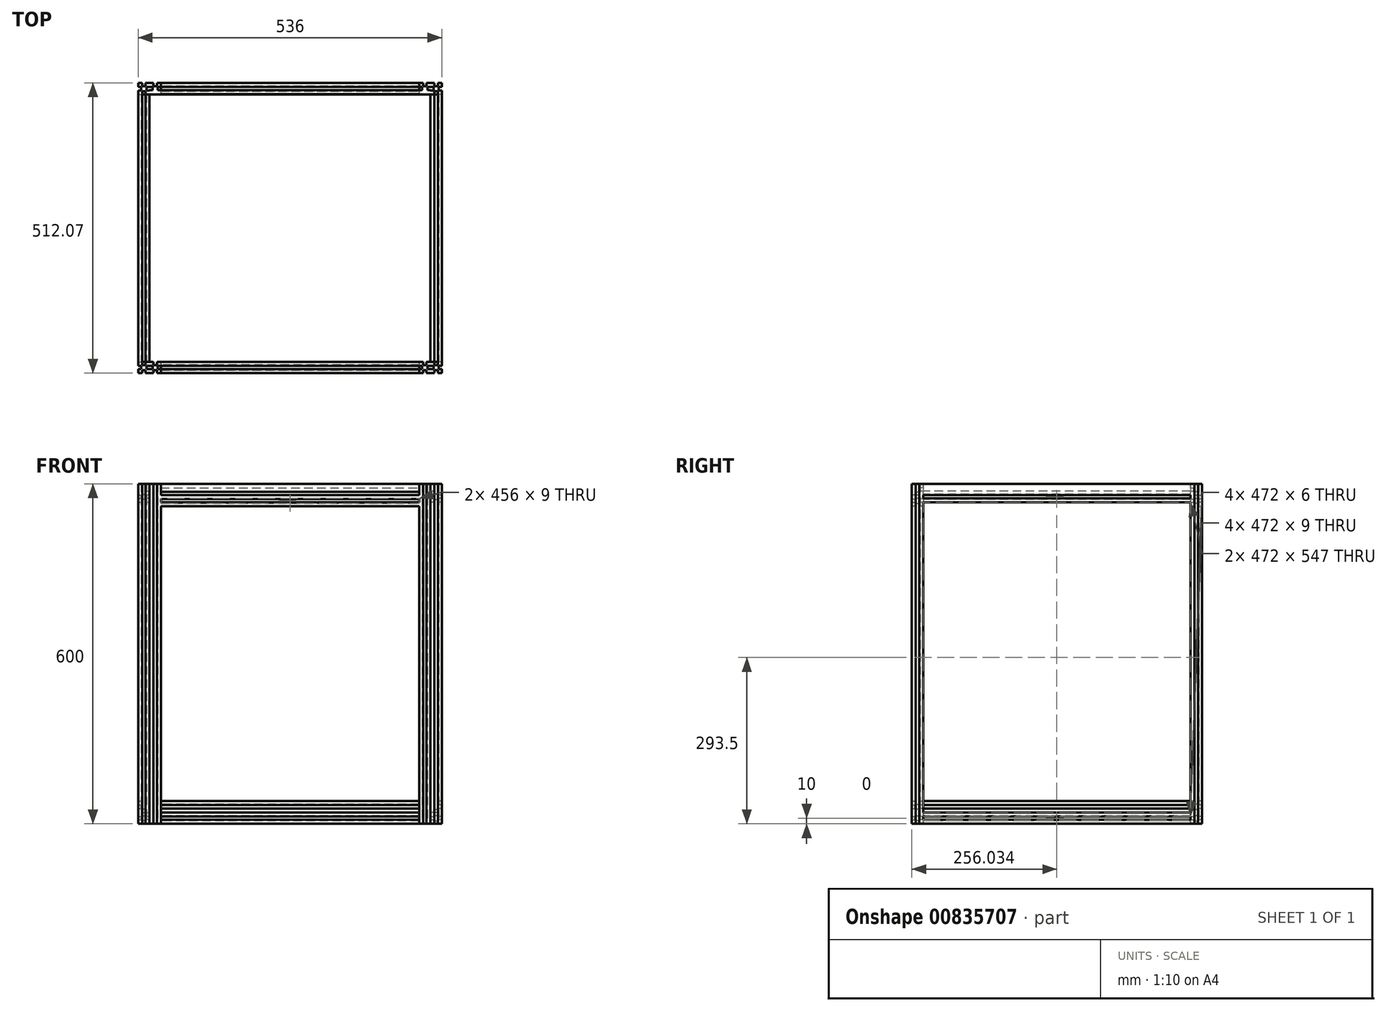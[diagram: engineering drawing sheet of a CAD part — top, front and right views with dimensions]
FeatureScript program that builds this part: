
annotation { "Feature Type Name" : "Feature", "Feature Type Description" : "" }
export const myFeature = defineFeature(function(context is Context, id is Id, definition is map)
    precondition{}
    {
        {
            var Q0;
            Q0=qCreatedBy(makeId("Right.planeOp"),FACE);
            var sketch = newSketch(context, id + "F0", { "sketchPlane" : qUnion([Q0])});
            skLineSegment(sketch, "E0.bottom", {"start": v(-73.97, 127.1) * mm, "end": v(-53.97, 127.1) * mm});
            skLineSegment(sketch, "E0.top", {"start": v(-73.97, 147.1) * mm, "end": v(-53.97, 147.1) * mm});
            skLineSegment(sketch, "E0.left", {"start": v(-73.97, 127.1) * mm, "end": v(-73.97, 147.1) * mm});
            skLineSegment(sketch, "E0.right", {"start": v(-53.97, 127.1) * mm, "end": v(-53.97, 147.1) * mm});
            skLineSegment(sketch, "E1.bottom", {"start": v(-66.97, 147.1) * mm, "end": v(-60.97, 147.1) * mm});
            skLineSegment(sketch, "E1.top", {"start": v(-66.97, 141.6) * mm, "end": v(-60.97, 141.6) * mm});
            skLineSegment(sketch, "E1.left", {"start": v(-66.97, 147.1) * mm, "end": v(-66.97, 141.6) * mm});
            skLineSegment(sketch, "E1.right", {"start": v(-60.97, 147.1) * mm, "end": v(-60.97, 141.6) * mm});
            skLineSegment(sketch, "E2.bottom", {"start": v(-53.97, 140.1) * mm, "end": v(-59.47, 140.1) * mm});
            skLineSegment(sketch, "E2.top", {"start": v(-53.97, 134.1) * mm, "end": v(-59.47, 134.1) * mm});
            skLineSegment(sketch, "E2.left", {"start": v(-53.97, 140.1) * mm, "end": v(-53.97, 134.1) * mm});
            skLineSegment(sketch, "E2.right", {"start": v(-59.47, 140.1) * mm, "end": v(-59.47, 134.1) * mm});
            skLineSegment(sketch, "E3.bottom", {"start": v(-60.97, 127.1) * mm, "end": v(-66.97, 127.1) * mm});
            skLineSegment(sketch, "E3.top", {"start": v(-60.97, 132.6) * mm, "end": v(-66.97, 132.6) * mm});
            skLineSegment(sketch, "E3.left", {"start": v(-60.97, 127.1) * mm, "end": v(-60.97, 132.6) * mm});
            skLineSegment(sketch, "E3.right", {"start": v(-66.97, 127.1) * mm, "end": v(-66.97, 132.6) * mm});
            skLineSegment(sketch, "E4.bottom", {"start": v(-73.97, 134.1) * mm, "end": v(-68.47, 134.1) * mm});
            skLineSegment(sketch, "E4.top", {"start": v(-73.97, 140.1) * mm, "end": v(-68.47, 140.1) * mm});
            skLineSegment(sketch, "E4.left", {"start": v(-73.97, 134.1) * mm, "end": v(-73.97, 140.1) * mm});
            skLineSegment(sketch, "E4.right", {"start": v(-68.47, 134.1) * mm, "end": v(-68.47, 140.1) * mm});
            skLineSegment(sketch, "E5.bottom", {"start": v(-74.01, 107.1) * mm, "end": v(-54.01, 107.1) * mm});
            skLineSegment(sketch, "E5.top", {"start": v(-74.01, 127.1) * mm, "end": v(-54.01, 127.1) * mm});
            skLineSegment(sketch, "E5.left", {"start": v(-74.01, 107.1) * mm, "end": v(-74.01, 127.1) * mm});
            skLineSegment(sketch, "E5.right", {"start": v(-54.01, 107.1) * mm, "end": v(-54.01, 127.1) * mm});
            skLineSegment(sketch, "E6.bottom", {"start": v(-67.01, 127.1) * mm, "end": v(-61.01, 127.1) * mm});
            skLineSegment(sketch, "E6.top", {"start": v(-67.01, 121.6) * mm, "end": v(-61.01, 121.6) * mm});
            skLineSegment(sketch, "E6.left", {"start": v(-67.01, 127.1) * mm, "end": v(-67.01, 121.6) * mm});
            skLineSegment(sketch, "E6.right", {"start": v(-61.01, 127.1) * mm, "end": v(-61.01, 121.6) * mm});
            skLineSegment(sketch, "E7.bottom", {"start": v(-54.01, 120.1) * mm, "end": v(-59.51, 120.1) * mm});
            skLineSegment(sketch, "E7.top", {"start": v(-54.01, 114.1) * mm, "end": v(-59.51, 114.1) * mm});
            skLineSegment(sketch, "E7.left", {"start": v(-54.01, 120.1) * mm, "end": v(-54.01, 114.1) * mm});
            skLineSegment(sketch, "E7.right", {"start": v(-59.51, 120.1) * mm, "end": v(-59.51, 114.1) * mm});
            skLineSegment(sketch, "E8.bottom", {"start": v(-61.01, 107.1) * mm, "end": v(-67.01, 107.1) * mm});
            skLineSegment(sketch, "E8.top", {"start": v(-61.01, 112.6) * mm, "end": v(-67.01, 112.6) * mm});
            skLineSegment(sketch, "E8.left", {"start": v(-61.01, 107.1) * mm, "end": v(-61.01, 112.6) * mm});
            skLineSegment(sketch, "E8.right", {"start": v(-67.01, 107.1) * mm, "end": v(-67.01, 112.6) * mm});
            skLineSegment(sketch, "E9.bottom", {"start": v(-74.01, 114.1) * mm, "end": v(-68.51, 114.1) * mm});
            skLineSegment(sketch, "E9.top", {"start": v(-74.01, 120.1) * mm, "end": v(-68.51, 120.1) * mm});
            skLineSegment(sketch, "E9.left", {"start": v(-74.01, 114.1) * mm, "end": v(-74.01, 120.1) * mm});
            skLineSegment(sketch, "E9.right", {"start": v(-68.51, 114.1) * mm, "end": v(-68.51, 120.1) * mm});
            skSolve(sketch);
        }
        {
            var Q0;
            {var subQ11=sQuery(id+"F0.wireOp",EDGE,"E0.bottom");Q0=makeQuery(id+"F0.imprint","IMPRINT",FACE,{"disambiguationData":[TD([[makeQuery(id+"F0.imprint","IMPRINT",EDGE,{"derivedFrom":subQ11}),1.0]])]});}
            var Q1;
            Q1=makeQuery(id+"F0.imprint","IMPRINT",FACE,{"disambiguationData":[TD([[makeQuery(id+"F0.imprint","IMPRINT",EDGE,{"derivedFrom":sQuery(id+"F0.wireOp",EDGE,"E6.top")}),-1.0]])]});
            extrude(context, id + "F1", {"entities" : qUnion([Q0, Q1]), "depth" : 270 * mm, "offsetDistance" : 25 * mm});
        }
        {
            var Q0;
            {var subQ0=sQuery(id+"F0.wireOp",EDGE,"E5.bottom");var subQ1=makeQuery(id+"F1.opExtrude","SWEPT_FACE",FACE,{"disambiguationData":[OSD([subQ0]),TDD([makeQuery(id+"F0.imprint","IMPRINT",EDGE,{"disambiguationData":[TD([[makeQuery(id+"F0.imprint","INTERSECT",VERTEX,{"derivedFrom":[subQ0,sQuery(id+"F0.wireOp",EDGE,"E5.left")]}),-1.0]])],"derivedFrom":subQ0})])]});Q0=makeQuery(id+"FbfQmAbu5wMZM1G_1.boolean.opBoolean","MERGE",FACE,{"derivedFrom":[subQ1,makeQuery(id+"FbfQmAbu5wMZM1G_1.opPattern","COPY",FACE,{"derivedFrom":subQ1,"instanceName":"1"})]});}
            var sketch = newSketch(context, id + "F2", { "sketchPlane" : qUnion([Q0])});
            skLineSegment(sketch, "E10.bottom", {"start": v(290, 54.12) * mm, "end": v(290, 74.12) * mm});
            skLineSegment(sketch, "E10.top", {"start": v(270, 54.12) * mm, "end": v(270, 74.12) * mm});
            skLineSegment(sketch, "E10.left", {"start": v(290, 54.12) * mm, "end": v(270, 54.12) * mm});
            skLineSegment(sketch, "E10.right", {"start": v(290, 74.12) * mm, "end": v(270, 74.12) * mm});
            skLineSegment(sketch, "E11.bottom", {"start": v(270, 61.12) * mm, "end": v(270, 67.12) * mm});
            skLineSegment(sketch, "E11.top", {"start": v(275.5, 61.12) * mm, "end": v(275.5, 67.12) * mm});
            skLineSegment(sketch, "E11.left", {"start": v(270, 61.12) * mm, "end": v(275.5, 61.12) * mm});
            skLineSegment(sketch, "E11.right", {"start": v(270, 67.12) * mm, "end": v(275.5, 67.12) * mm});
            skLineSegment(sketch, "E12.bottom", {"start": v(277, 74.12) * mm, "end": v(277, 68.62) * mm});
            skLineSegment(sketch, "E12.top", {"start": v(283, 74.12) * mm, "end": v(283, 68.62) * mm});
            skLineSegment(sketch, "E12.left", {"start": v(277, 74.12) * mm, "end": v(283, 74.12) * mm});
            skLineSegment(sketch, "E12.right", {"start": v(277, 68.62) * mm, "end": v(283, 68.62) * mm});
            skLineSegment(sketch, "E13.bottom", {"start": v(290, 67.12) * mm, "end": v(290, 61.12) * mm});
            skLineSegment(sketch, "E13.top", {"start": v(284.5, 67.12) * mm, "end": v(284.5, 61.12) * mm});
            skLineSegment(sketch, "E13.left", {"start": v(290, 67.12) * mm, "end": v(284.5, 67.12) * mm});
            skLineSegment(sketch, "E13.right", {"start": v(290, 61.12) * mm, "end": v(284.5, 61.12) * mm});
            skLineSegment(sketch, "E14.bottom", {"start": v(283, 54.12) * mm, "end": v(283, 59.62) * mm});
            skLineSegment(sketch, "E14.top", {"start": v(277, 54.12) * mm, "end": v(277, 59.62) * mm});
            skLineSegment(sketch, "E14.left", {"start": v(283, 54.12) * mm, "end": v(277, 54.12) * mm});
            skLineSegment(sketch, "E14.right", {"start": v(283, 59.62) * mm, "end": v(277, 59.62) * mm});
            skLineSegment(sketch, "E15.bottom", {"start": v(310, 54.09) * mm, "end": v(310, 74.09) * mm});
            skLineSegment(sketch, "E15.top", {"start": v(290, 54.09) * mm, "end": v(290, 74.09) * mm});
            skLineSegment(sketch, "E15.left", {"start": v(310, 54.09) * mm, "end": v(290, 54.09) * mm});
            skLineSegment(sketch, "E15.right", {"start": v(310, 74.09) * mm, "end": v(290, 74.09) * mm});
            skLineSegment(sketch, "E16.bottom", {"start": v(290, 61.09) * mm, "end": v(290, 67.09) * mm});
            skLineSegment(sketch, "E16.top", {"start": v(295.5, 61.09) * mm, "end": v(295.5, 67.09) * mm});
            skLineSegment(sketch, "E16.left", {"start": v(290, 61.09) * mm, "end": v(295.5, 61.09) * mm});
            skLineSegment(sketch, "E16.right", {"start": v(290, 67.09) * mm, "end": v(295.5, 67.09) * mm});
            skLineSegment(sketch, "E17.bottom", {"start": v(297, 74.09) * mm, "end": v(297, 68.59) * mm});
            skLineSegment(sketch, "E17.top", {"start": v(303, 74.09) * mm, "end": v(303, 68.59) * mm});
            skLineSegment(sketch, "E17.left", {"start": v(297, 74.09) * mm, "end": v(303, 74.09) * mm});
            skLineSegment(sketch, "E17.right", {"start": v(297, 68.59) * mm, "end": v(303, 68.59) * mm});
            skLineSegment(sketch, "E18.bottom", {"start": v(310, 67.09) * mm, "end": v(310, 61.09) * mm});
            skLineSegment(sketch, "E18.top", {"start": v(304.5, 67.09) * mm, "end": v(304.5, 61.09) * mm});
            skLineSegment(sketch, "E18.left", {"start": v(310, 67.09) * mm, "end": v(304.5, 67.09) * mm});
            skLineSegment(sketch, "E18.right", {"start": v(310, 61.09) * mm, "end": v(304.5, 61.09) * mm});
            skLineSegment(sketch, "E19.bottom", {"start": v(303, 54.09) * mm, "end": v(303, 59.59) * mm});
            skLineSegment(sketch, "E19.top", {"start": v(297, 54.09) * mm, "end": v(297, 59.59) * mm});
            skLineSegment(sketch, "E19.left", {"start": v(303, 54.09) * mm, "end": v(297, 54.09) * mm});
            skLineSegment(sketch, "E19.right", {"start": v(303, 59.59) * mm, "end": v(297, 59.59) * mm});
            skSolve(sketch);
        }
        {
            var Q0;
            Q0=makeQuery(id+"F2.imprint","IMPRINT",FACE,{"disambiguationData":[TD([[makeQuery(id+"F2.imprint","IMPRINT",EDGE,{"derivedFrom":sQuery(id+"F2.wireOp",EDGE,"E16.top")}),-1.0]])]});
            var Q1;
            {var subQ16=sQuery(id+"F2.wireOp",EDGE,"E10.bottom");Q1=makeQuery(id+"F2.imprint","IMPRINT",FACE,{"disambiguationData":[TD([[makeQuery(id+"F2.imprint","IMPRINT",EDGE,{"derivedFrom":subQ16}),1.0]])]});}
            extrude(context, id + "F3", {"entities" : qUnion([Q0, Q1]), "operationType" : NewBodyOperationType.ADD, "oppositeDirection" : true, "depth" : 600 * mm, "offsetDistance" : 25 * mm});
        }
        {
            var Q0;
            {var subQ1=sQuery(id+"F2.wireOp",EDGE,"E10.left");var subQ2=sQuery(id+"F2.wireOp",EDGE,"E10.top");var subQ3=makeQuery(id+"F2.imprint","INTERSECT",VERTEX,{"derivedFrom":[subQ2,subQ1]});var subQ5=sQuery(id+"F0.wireOp",EDGE,"E1.top");Q0=makeQuery(id+"F3.boolean.opBoolean","SPLIT",FACE,{"disambiguationData":[TD([makeQuery(id+"F1.opExtrude","SWEPT_FACE",FACE,{"disambiguationData":[OSD([subQ5])]})])],"derivedFrom":makeQuery(id+"F3.opExtrude","SWEPT_FACE",FACE,{"disambiguationData":[OSD([subQ2]),TDD([makeQuery(id+"F2.imprint","IMPRINT",EDGE,{"disambiguationData":[TD([[subQ3,-1.0]])],"derivedFrom":subQ2})])]})});}
            var sketch = newSketch(context, id + "F4", { "sketchPlane" : qUnion([Q0])});
            skLineSegment(sketch, "E20.bottom", {"start": v(54.16, 687.1) * mm, "end": v(74.16, 687.1) * mm});
            skLineSegment(sketch, "E20.top", {"start": v(54.16, 707.1) * mm, "end": v(74.16, 707.1) * mm});
            skLineSegment(sketch, "E20.left", {"start": v(54.16, 687.1) * mm, "end": v(54.16, 707.1) * mm});
            skLineSegment(sketch, "E20.right", {"start": v(74.16, 687.1) * mm, "end": v(74.16, 707.1) * mm});
            skLineSegment(sketch, "E21.bottom", {"start": v(61.16, 707.1) * mm, "end": v(67.16, 707.1) * mm});
            skLineSegment(sketch, "E21.top", {"start": v(61.16, 701.6) * mm, "end": v(67.16, 701.6) * mm});
            skLineSegment(sketch, "E21.left", {"start": v(61.16, 707.1) * mm, "end": v(61.16, 701.6) * mm});
            skLineSegment(sketch, "E21.right", {"start": v(67.16, 707.1) * mm, "end": v(67.16, 701.6) * mm});
            skLineSegment(sketch, "E22.bottom", {"start": v(74.16, 700.1) * mm, "end": v(68.66, 700.1) * mm});
            skLineSegment(sketch, "E22.top", {"start": v(74.16, 694.1) * mm, "end": v(68.66, 694.1) * mm});
            skLineSegment(sketch, "E22.left", {"start": v(74.16, 700.1) * mm, "end": v(74.16, 694.1) * mm});
            skLineSegment(sketch, "E22.right", {"start": v(68.66, 700.1) * mm, "end": v(68.66, 694.1) * mm});
            skLineSegment(sketch, "E23.bottom", {"start": v(67.16, 687.1) * mm, "end": v(61.16, 687.1) * mm});
            skLineSegment(sketch, "E23.top", {"start": v(67.16, 692.6) * mm, "end": v(61.16, 692.6) * mm});
            skLineSegment(sketch, "E23.left", {"start": v(67.16, 687.1) * mm, "end": v(67.16, 692.6) * mm});
            skLineSegment(sketch, "E23.right", {"start": v(61.16, 687.1) * mm, "end": v(61.16, 692.6) * mm});
            skLineSegment(sketch, "E24.bottom", {"start": v(54.16, 694.1) * mm, "end": v(59.66, 694.1) * mm});
            skLineSegment(sketch, "E24.top", {"start": v(54.16, 700.1) * mm, "end": v(59.66, 700.1) * mm});
            skLineSegment(sketch, "E24.left", {"start": v(54.16, 694.1) * mm, "end": v(54.16, 700.1) * mm});
            skLineSegment(sketch, "E24.right", {"start": v(59.66, 694.1) * mm, "end": v(59.66, 700.1) * mm});
            skLineSegment(sketch, "E25.bottom", {"start": v(54.12, 667.1) * mm, "end": v(74.12, 667.1) * mm});
            skLineSegment(sketch, "E25.top", {"start": v(54.12, 687.1) * mm, "end": v(74.12, 687.1) * mm});
            skLineSegment(sketch, "E25.left", {"start": v(54.12, 667.1) * mm, "end": v(54.12, 687.1) * mm});
            skLineSegment(sketch, "E25.right", {"start": v(74.12, 667.1) * mm, "end": v(74.12, 687.1) * mm});
            skLineSegment(sketch, "E26.bottom", {"start": v(61.12, 687.1) * mm, "end": v(67.12, 687.1) * mm});
            skLineSegment(sketch, "E26.top", {"start": v(61.12, 681.6) * mm, "end": v(67.12, 681.6) * mm});
            skLineSegment(sketch, "E26.left", {"start": v(61.12, 687.1) * mm, "end": v(61.12, 681.6) * mm});
            skLineSegment(sketch, "E26.right", {"start": v(67.12, 687.1) * mm, "end": v(67.12, 681.6) * mm});
            skLineSegment(sketch, "E27.bottom", {"start": v(74.12, 680.1) * mm, "end": v(68.62, 680.1) * mm});
            skLineSegment(sketch, "E27.top", {"start": v(74.12, 674.1) * mm, "end": v(68.62, 674.1) * mm});
            skLineSegment(sketch, "E27.left", {"start": v(74.12, 680.1) * mm, "end": v(74.12, 674.1) * mm});
            skLineSegment(sketch, "E27.right", {"start": v(68.62, 680.1) * mm, "end": v(68.62, 674.1) * mm});
            skLineSegment(sketch, "E28.bottom", {"start": v(67.12, 667.1) * mm, "end": v(61.12, 667.1) * mm});
            skLineSegment(sketch, "E28.top", {"start": v(67.12, 672.6) * mm, "end": v(61.12, 672.6) * mm});
            skLineSegment(sketch, "E28.left", {"start": v(67.12, 667.1) * mm, "end": v(67.12, 672.6) * mm});
            skLineSegment(sketch, "E28.right", {"start": v(61.12, 667.1) * mm, "end": v(61.12, 672.6) * mm});
            skLineSegment(sketch, "E29.bottom", {"start": v(54.12, 674.1) * mm, "end": v(59.62, 674.1) * mm});
            skLineSegment(sketch, "E29.top", {"start": v(54.12, 680.1) * mm, "end": v(59.62, 680.1) * mm});
            skLineSegment(sketch, "E29.left", {"start": v(54.12, 674.1) * mm, "end": v(54.12, 680.1) * mm});
            skLineSegment(sketch, "E29.right", {"start": v(59.62, 674.1) * mm, "end": v(59.62, 680.1) * mm});
            skSolve(sketch);
        }
        {
            var Q0;
            {var subQ10=sQuery(id+"F4.wireOp",EDGE,"E24.bottom");Q0=makeQuery(id+"F4.imprint","IMPRINT",FACE,{"disambiguationData":[TD([[makeQuery(id+"F4.imprint","IMPRINT",EDGE,{"derivedFrom":subQ10}),-1.0]])]});}
            var Q1;
            {var subQ20=sQuery(id+"F4.wireOp",EDGE,"E20.bottom");Q1=makeQuery(id+"F4.imprint","IMPRINT",FACE,{"disambiguationData":[TD([[makeQuery(id+"F4.imprint","IMPRINT",EDGE,{"derivedFrom":subQ20}),1.0]])]});}
            var Q2;
            {var subQ6=sQuery(id+"F4.wireOp",EDGE,"E26.top");Q2=makeQuery(id+"F4.imprint","IMPRINT",FACE,{"disambiguationData":[TD([[makeQuery(id+"F4.imprint","IMPRINT",EDGE,{"derivedFrom":subQ6}),-1.0]])]});}
            var Q3;
            {var subQ2=sQuery(id+"F4.wireOp",EDGE,"E26.left");Q3=makeQuery(id+"F4.imprint","IMPRINT",FACE,{"disambiguationData":[TD([[makeQuery(id+"F4.imprint","IMPRINT",EDGE,{"derivedFrom":subQ2}),-1.0]])]});}
            extrude(context, id + "F5", {"entities" : qUnion([Q0, Q1, Q2, Q3]), "operationType" : NewBodyOperationType.ADD, "depth" : 228 * mm, "offsetDistance" : 25 * mm});
        }
        {
            var Q0;
            {var subQ0=sQuery(id+"F2.wireOp",EDGE,"E15.left");Q0=makeQuery(id+"F3.opExtrude","SWEPT_FACE",FACE,{"disambiguationData":[OSD([subQ0]),TDD([makeQuery(id+"F2.imprint","IMPRINT",EDGE,{"disambiguationData":[TD([[makeQuery(id+"F2.imprint","INTERSECT",VERTEX,{"derivedFrom":[sQuery(id+"F2.wireOp",EDGE,"E15.bottom"),subQ0]}),-1.0]])],"derivedFrom":subQ0})])]});}
            var sketch = newSketch(context, id + "F6", { "sketchPlane" : qUnion([Q0])});
            skLineSegment(sketch, "E30.bottom", {"start": v(-309.96, 694.1) * mm, "end": v(-289.96, 694.1) * mm});
            skLineSegment(sketch, "E31.bottom", {"start": v(-296.96, 694.1) * mm, "end": v(-302.96, 694.1) * mm});
            skLineSegment(sketch, "E32.bottom", {"start": v(-310, 674.1) * mm, "end": v(-290, 674.1) * mm});
            skLineSegment(sketch, "E32.top", {"start": v(-310, 694.1) * mm, "end": v(-290, 694.1) * mm});
            skLineSegment(sketch, "E32.left", {"start": v(-310, 674.1) * mm, "end": v(-310, 694.1) * mm});
            skLineSegment(sketch, "E32.right", {"start": v(-290, 674.1) * mm, "end": v(-290, 694.1) * mm});
            skLineSegment(sketch, "E33.bottom", {"start": v(-303, 694.1) * mm, "end": v(-297, 694.1) * mm});
            skLineSegment(sketch, "E33.top", {"start": v(-303, 688.6) * mm, "end": v(-297, 688.6) * mm});
            skLineSegment(sketch, "E33.left", {"start": v(-303, 694.1) * mm, "end": v(-303, 688.6) * mm});
            skLineSegment(sketch, "E33.right", {"start": v(-297, 694.1) * mm, "end": v(-297, 688.6) * mm});
            skLineSegment(sketch, "E34.bottom", {"start": v(-290, 687.1) * mm, "end": v(-295.5, 687.1) * mm});
            skLineSegment(sketch, "E34.top", {"start": v(-290, 681.1) * mm, "end": v(-295.5, 681.1) * mm});
            skLineSegment(sketch, "E34.left", {"start": v(-290, 687.1) * mm, "end": v(-290, 681.1) * mm});
            skLineSegment(sketch, "E34.right", {"start": v(-295.5, 687.1) * mm, "end": v(-295.5, 681.1) * mm});
            skLineSegment(sketch, "E35.bottom", {"start": v(-297, 674.1) * mm, "end": v(-303, 674.1) * mm});
            skLineSegment(sketch, "E35.top", {"start": v(-297, 679.6) * mm, "end": v(-303, 679.6) * mm});
            skLineSegment(sketch, "E35.left", {"start": v(-297, 674.1) * mm, "end": v(-297, 679.6) * mm});
            skLineSegment(sketch, "E35.right", {"start": v(-303, 674.1) * mm, "end": v(-303, 679.6) * mm});
            skLineSegment(sketch, "E36.bottom", {"start": v(-310, 681.1) * mm, "end": v(-304.5, 681.1) * mm});
            skLineSegment(sketch, "E36.top", {"start": v(-310, 687.1) * mm, "end": v(-304.5, 687.1) * mm});
            skLineSegment(sketch, "E36.left", {"start": v(-310, 681.1) * mm, "end": v(-310, 687.1) * mm});
            skLineSegment(sketch, "E36.right", {"start": v(-304.5, 681.1) * mm, "end": v(-304.5, 687.1) * mm});
            skLineSegment(sketch, "E37.bottom", {"start": v(-309.96, 127.1) * mm, "end": v(-289.96, 127.1) * mm});
            skLineSegment(sketch, "E37.top", {"start": v(-309.96, 147.1) * mm, "end": v(-289.96, 147.1) * mm});
            skLineSegment(sketch, "E37.left", {"start": v(-309.96, 127.1) * mm, "end": v(-309.96, 147.1) * mm});
            skLineSegment(sketch, "E37.right", {"start": v(-289.96, 127.1) * mm, "end": v(-289.96, 147.1) * mm});
            skLineSegment(sketch, "E38.bottom", {"start": v(-302.96, 147.1) * mm, "end": v(-296.96, 147.1) * mm});
            skLineSegment(sketch, "E38.top", {"start": v(-302.96, 141.6) * mm, "end": v(-296.96, 141.6) * mm});
            skLineSegment(sketch, "E38.left", {"start": v(-302.96, 147.1) * mm, "end": v(-302.96, 141.6) * mm});
            skLineSegment(sketch, "E38.right", {"start": v(-296.96, 147.1) * mm, "end": v(-296.96, 141.6) * mm});
            skLineSegment(sketch, "E39.bottom", {"start": v(-289.96, 140.1) * mm, "end": v(-295.46, 140.1) * mm});
            skLineSegment(sketch, "E39.top", {"start": v(-289.96, 134.1) * mm, "end": v(-295.46, 134.1) * mm});
            skLineSegment(sketch, "E39.left", {"start": v(-289.96, 140.1) * mm, "end": v(-289.96, 134.1) * mm});
            skLineSegment(sketch, "E39.right", {"start": v(-295.46, 140.1) * mm, "end": v(-295.46, 134.1) * mm});
            skLineSegment(sketch, "E40.bottom", {"start": v(-296.96, 127.1) * mm, "end": v(-302.96, 127.1) * mm});
            skLineSegment(sketch, "E40.top", {"start": v(-296.96, 132.6) * mm, "end": v(-302.96, 132.6) * mm});
            skLineSegment(sketch, "E40.left", {"start": v(-296.96, 127.1) * mm, "end": v(-296.96, 132.6) * mm});
            skLineSegment(sketch, "E40.right", {"start": v(-302.96, 127.1) * mm, "end": v(-302.96, 132.6) * mm});
            skLineSegment(sketch, "E41.bottom", {"start": v(-309.96, 134.1) * mm, "end": v(-304.46, 134.1) * mm});
            skLineSegment(sketch, "E41.top", {"start": v(-309.96, 140.1) * mm, "end": v(-304.46, 140.1) * mm});
            skLineSegment(sketch, "E41.left", {"start": v(-309.96, 134.1) * mm, "end": v(-309.96, 140.1) * mm});
            skLineSegment(sketch, "E41.right", {"start": v(-304.46, 134.1) * mm, "end": v(-304.46, 140.1) * mm});
            skLineSegment(sketch, "E42.bottom", {"start": v(-310, 107.1) * mm, "end": v(-290, 107.1) * mm});
            skLineSegment(sketch, "E42.top", {"start": v(-310, 127.1) * mm, "end": v(-290, 127.1) * mm});
            skLineSegment(sketch, "E42.left", {"start": v(-310, 107.1) * mm, "end": v(-310, 127.1) * mm});
            skLineSegment(sketch, "E42.right", {"start": v(-290, 107.1) * mm, "end": v(-290, 127.1) * mm});
            skLineSegment(sketch, "E43.bottom", {"start": v(-303, 127.1) * mm, "end": v(-297, 127.1) * mm});
            skLineSegment(sketch, "E43.top", {"start": v(-303, 121.6) * mm, "end": v(-297, 121.6) * mm});
            skLineSegment(sketch, "E43.left", {"start": v(-303, 127.1) * mm, "end": v(-303, 121.6) * mm});
            skLineSegment(sketch, "E43.right", {"start": v(-297, 127.1) * mm, "end": v(-297, 121.6) * mm});
            skLineSegment(sketch, "E44.bottom", {"start": v(-290, 120.1) * mm, "end": v(-295.5, 120.1) * mm});
            skLineSegment(sketch, "E44.top", {"start": v(-290, 114.1) * mm, "end": v(-295.5, 114.1) * mm});
            skLineSegment(sketch, "E44.left", {"start": v(-290, 120.1) * mm, "end": v(-290, 114.1) * mm});
            skLineSegment(sketch, "E44.right", {"start": v(-295.5, 120.1) * mm, "end": v(-295.5, 114.1) * mm});
            skLineSegment(sketch, "E45.bottom", {"start": v(-297, 107.1) * mm, "end": v(-303, 107.1) * mm});
            skLineSegment(sketch, "E45.top", {"start": v(-297, 112.6) * mm, "end": v(-303, 112.6) * mm});
            skLineSegment(sketch, "E45.left", {"start": v(-297, 107.1) * mm, "end": v(-297, 112.6) * mm});
            skLineSegment(sketch, "E45.right", {"start": v(-303, 107.1) * mm, "end": v(-303, 112.6) * mm});
            skLineSegment(sketch, "E46.bottom", {"start": v(-310, 114.1) * mm, "end": v(-304.5, 114.1) * mm});
            skLineSegment(sketch, "E46.top", {"start": v(-310, 120.1) * mm, "end": v(-304.5, 120.1) * mm});
            skLineSegment(sketch, "E46.left", {"start": v(-310, 114.1) * mm, "end": v(-310, 120.1) * mm});
            skLineSegment(sketch, "E46.right", {"start": v(-304.5, 114.1) * mm, "end": v(-304.5, 120.1) * mm});
            skSolve(sketch);
        }
        {
            var Q0;
            {var subQ13=sQuery(id+"F6.wireOp",EDGE,"E37.bottom");Q0=makeQuery(id+"F6.imprint","IMPRINT",FACE,{"disambiguationData":[TD([[makeQuery(id+"F6.imprint","IMPRINT",EDGE,{"derivedFrom":subQ13}),1.0]])]});}
            var Q1;
            {var subQ5=sQuery(id+"F6.wireOp",EDGE,"E41.bottom");Q1=makeQuery(id+"F6.imprint","IMPRINT",FACE,{"disambiguationData":[TD([[makeQuery(id+"F6.imprint","IMPRINT",EDGE,{"derivedFrom":subQ5}),-1.0]])]});}
            var Q2;
            {var subQ2=sQuery(id+"F6.wireOp",EDGE,"E43.left");Q2=makeQuery(id+"F6.imprint","IMPRINT",FACE,{"disambiguationData":[TD([[makeQuery(id+"F6.imprint","IMPRINT",EDGE,{"derivedFrom":subQ2}),-1.0]])]});}
            var Q3;
            {var subQ6=sQuery(id+"F6.wireOp",EDGE,"E43.top");Q3=makeQuery(id+"F6.imprint","IMPRINT",FACE,{"disambiguationData":[TD([[makeQuery(id+"F6.imprint","IMPRINT",EDGE,{"derivedFrom":subQ6}),-1.0]])]});}
            var Q4;
            {var subQ12=sQuery(id+"F6.wireOp",EDGE,"9667445b-14a2-414e-8e40-848a2c53a070.bottom");Q4=makeQuery(id+"F6.imprint","IMPRINT",FACE,{"disambiguationData":[TD([[makeQuery(id+"F6.imprint","IMPRINT",EDGE,{"derivedFrom":subQ12}),-1.0]])]});}
            var Q5;
            {var subQ13=sQuery(id+"F6.wireOp",EDGE,"E30.bottom");Q5=makeQuery(id+"F6.imprint","IMPRINT",FACE,{"disambiguationData":[TD([[makeQuery(id+"F6.imprint","IMPRINT",EDGE,{"derivedFrom":subQ13}),1.0]])]});}
            var Q6;
            {var subQ6=sQuery(id+"F6.wireOp",EDGE,"E33.top");Q6=makeQuery(id+"F6.imprint","IMPRINT",FACE,{"disambiguationData":[TD([[makeQuery(id+"F6.imprint","IMPRINT",EDGE,{"derivedFrom":subQ6}),-1.0]])]});}
            var Q7;
            {var subQ2=sQuery(id+"F6.wireOp",EDGE,"E33.left");Q7=makeQuery(id+"F6.imprint","IMPRINT",FACE,{"disambiguationData":[TD([[makeQuery(id+"F6.imprint","IMPRINT",EDGE,{"derivedFrom":subQ2}),-1.0]])]});}
            extrude(context, id + "F7", {"entities" : qUnion([Q0, Q1, Q2, Q3, Q4, Q5, Q6, Q7]), "operationType" : NewBodyOperationType.ADD, "depth" : 236 * mm, "offsetDistance" : 25 * mm});
        }
        {
            var Q0;
            Q0=makeQuery(id+"F1.opExtrude","SWEPT_BODY",BODY,{"disambiguationData":[OSD([sQuery(id+"F0.wireOp",EDGE,"E0.bottom"),sQuery(id+"F0.wireOp",EDGE,"E0.top"),sQuery(id+"F0.wireOp",EDGE,"E0.left"),sQuery(id+"F0.wireOp",EDGE,"E0.right"),sQuery(id+"F0.wireOp",EDGE,"E1.top"),sQuery(id+"F0.wireOp",EDGE,"E1.left"),sQuery(id+"F0.wireOp",EDGE,"E1.right"),sQuery(id+"F0.wireOp",EDGE,"E2.bottom"),sQuery(id+"F0.wireOp",EDGE,"E2.top"),sQuery(id+"F0.wireOp",EDGE,"E2.right"),sQuery(id+"F0.wireOp",EDGE,"E3.top"),sQuery(id+"F0.wireOp",EDGE,"E3.left"),sQuery(id+"F0.wireOp",EDGE,"E3.right"),sQuery(id+"F0.wireOp",EDGE,"E4.bottom"),sQuery(id+"F0.wireOp",EDGE,"E4.top"),sQuery(id+"F0.wireOp",EDGE,"E4.right"),sQuery(id+"F0.wireOp",EDGE,"E5.bottom"),sQuery(id+"F0.wireOp",EDGE,"E5.top"),sQuery(id+"F0.wireOp",EDGE,"E5.left"),sQuery(id+"F0.wireOp",EDGE,"E5.right"),sQuery(id+"F0.wireOp",EDGE,"E6.bottom"),sQuery(id+"F0.wireOp",EDGE,"E6.top"),sQuery(id+"F0.wireOp",EDGE,"E6.left"),sQuery(id+"F0.wireOp",EDGE,"E6.right"),sQuery(id+"F0.wireOp",EDGE,"E7.bottom"),sQuery(id+"F0.wireOp",EDGE,"E7.top"),sQuery(id+"F0.wireOp",EDGE,"E7.right"),sQuery(id+"F0.wireOp",EDGE,"E8.top"),sQuery(id+"F0.wireOp",EDGE,"E8.left"),sQuery(id+"F0.wireOp",EDGE,"E8.right"),sQuery(id+"F0.wireOp",EDGE,"E9.bottom"),sQuery(id+"F0.wireOp",EDGE,"E9.top"),sQuery(id+"F0.wireOp",EDGE,"E9.right")])]});
            var Q1;
            Q1=makeQuery(id+"F7.opExtrude","CAP_FACE",FACE,{"disambiguationData":[OSD([sQuery(id+"F6.wireOp",EDGE,"E30.bottom"),sQuery(id+"F6.wireOp",EDGE,"E30.top"),sQuery(id+"F6.wireOp",EDGE,"E30.left"),sQuery(id+"F6.wireOp",EDGE,"E30.right"),sQuery(id+"F6.wireOp",EDGE,"697817fb-edbd-40a5-a29d-952f93a9c78b.top"),sQuery(id+"F6.wireOp",EDGE,"697817fb-edbd-40a5-a29d-952f93a9c78b.left"),sQuery(id+"F6.wireOp",EDGE,"697817fb-edbd-40a5-a29d-952f93a9c78b.right"),sQuery(id+"F6.wireOp",EDGE,"15fd4d5f-bd60-4fe3-bdb7-a61c8bb0770d.bottom"),sQuery(id+"F6.wireOp",EDGE,"15fd4d5f-bd60-4fe3-bdb7-a61c8bb0770d.top"),sQuery(id+"F6.wireOp",EDGE,"15fd4d5f-bd60-4fe3-bdb7-a61c8bb0770d.right"),sQuery(id+"F6.wireOp",EDGE,"E31.top"),sQuery(id+"F6.wireOp",EDGE,"E31.left"),sQuery(id+"F6.wireOp",EDGE,"E31.right"),sQuery(id+"F6.wireOp",EDGE,"9667445b-14a2-414e-8e40-848a2c53a070.bottom"),sQuery(id+"F6.wireOp",EDGE,"9667445b-14a2-414e-8e40-848a2c53a070.top"),sQuery(id+"F6.wireOp",EDGE,"9667445b-14a2-414e-8e40-848a2c53a070.right"),sQuery(id+"F6.wireOp",EDGE,"E32.bottom"),sQuery(id+"F6.wireOp",EDGE,"E32.top"),sQuery(id+"F6.wireOp",EDGE,"E32.left"),sQuery(id+"F6.wireOp",EDGE,"E32.right"),sQuery(id+"F6.wireOp",EDGE,"E33.bottom"),sQuery(id+"F6.wireOp",EDGE,"E33.top"),sQuery(id+"F6.wireOp",EDGE,"E33.left"),sQuery(id+"F6.wireOp",EDGE,"E33.right"),sQuery(id+"F6.wireOp",EDGE,"E34.bottom"),sQuery(id+"F6.wireOp",EDGE,"E34.top"),sQuery(id+"F6.wireOp",EDGE,"E34.right"),sQuery(id+"F6.wireOp",EDGE,"E35.top"),sQuery(id+"F6.wireOp",EDGE,"E35.left"),sQuery(id+"F6.wireOp",EDGE,"E35.right"),sQuery(id+"F6.wireOp",EDGE,"E36.bottom"),sQuery(id+"F6.wireOp",EDGE,"E36.top"),sQuery(id+"F6.wireOp",EDGE,"E36.right")])],"isStart":false});
            mirror(context, id + "F8", {"operationType" : NewBodyOperationType.ADD, "entities" : qUnion([Q0]), "mirrorPlane" : qUnion([Q1])});
        }
        {
            var Q0;
            Q0=makeQuery(id+"F1.opExtrude","SWEPT_BODY",BODY,{"disambiguationData":[OSD([sQuery(id+"F0.wireOp",EDGE,"E0.bottom"),sQuery(id+"F0.wireOp",EDGE,"E0.top"),sQuery(id+"F0.wireOp",EDGE,"E0.left"),sQuery(id+"F0.wireOp",EDGE,"E0.right"),sQuery(id+"F0.wireOp",EDGE,"E1.top"),sQuery(id+"F0.wireOp",EDGE,"E1.left"),sQuery(id+"F0.wireOp",EDGE,"E1.right"),sQuery(id+"F0.wireOp",EDGE,"E2.bottom"),sQuery(id+"F0.wireOp",EDGE,"E2.top"),sQuery(id+"F0.wireOp",EDGE,"E2.right"),sQuery(id+"F0.wireOp",EDGE,"E3.top"),sQuery(id+"F0.wireOp",EDGE,"E3.left"),sQuery(id+"F0.wireOp",EDGE,"E3.right"),sQuery(id+"F0.wireOp",EDGE,"E4.bottom"),sQuery(id+"F0.wireOp",EDGE,"E4.top"),sQuery(id+"F0.wireOp",EDGE,"E4.right"),sQuery(id+"F0.wireOp",EDGE,"E5.bottom"),sQuery(id+"F0.wireOp",EDGE,"E5.top"),sQuery(id+"F0.wireOp",EDGE,"E5.left"),sQuery(id+"F0.wireOp",EDGE,"E5.right"),sQuery(id+"F0.wireOp",EDGE,"E6.bottom"),sQuery(id+"F0.wireOp",EDGE,"E6.top"),sQuery(id+"F0.wireOp",EDGE,"E6.left"),sQuery(id+"F0.wireOp",EDGE,"E6.right"),sQuery(id+"F0.wireOp",EDGE,"E7.bottom"),sQuery(id+"F0.wireOp",EDGE,"E7.top"),sQuery(id+"F0.wireOp",EDGE,"E7.right"),sQuery(id+"F0.wireOp",EDGE,"E8.top"),sQuery(id+"F0.wireOp",EDGE,"E8.left"),sQuery(id+"F0.wireOp",EDGE,"E8.right"),sQuery(id+"F0.wireOp",EDGE,"E9.bottom"),sQuery(id+"F0.wireOp",EDGE,"E9.top"),sQuery(id+"F0.wireOp",EDGE,"E9.right")])]});
            var Q1;
            Q1=makeQuery(id+"F8.opPattern","COPY",FACE,{"derivedFrom":makeQuery(id+"F5.opExtrude","CAP_FACE",FACE,{"disambiguationData":[OSD([sQuery(id+"F4.wireOp",EDGE,"E20.bottom"),sQuery(id+"F4.wireOp",EDGE,"E20.top"),sQuery(id+"F4.wireOp",EDGE,"E20.left"),sQuery(id+"F4.wireOp",EDGE,"E20.right"),sQuery(id+"F4.wireOp",EDGE,"E21.top"),sQuery(id+"F4.wireOp",EDGE,"E21.left"),sQuery(id+"F4.wireOp",EDGE,"E21.right"),sQuery(id+"F4.wireOp",EDGE,"E22.bottom"),sQuery(id+"F4.wireOp",EDGE,"E22.top"),sQuery(id+"F4.wireOp",EDGE,"E22.right"),sQuery(id+"F4.wireOp",EDGE,"E23.top"),sQuery(id+"F4.wireOp",EDGE,"E23.left"),sQuery(id+"F4.wireOp",EDGE,"E23.right"),sQuery(id+"F4.wireOp",EDGE,"E24.bottom"),sQuery(id+"F4.wireOp",EDGE,"E24.top"),sQuery(id+"F4.wireOp",EDGE,"E24.right"),sQuery(id+"F4.wireOp",EDGE,"E25.bottom"),sQuery(id+"F4.wireOp",EDGE,"E25.top"),sQuery(id+"F4.wireOp",EDGE,"E25.left"),sQuery(id+"F4.wireOp",EDGE,"E25.right"),sQuery(id+"F4.wireOp",EDGE,"E26.bottom"),sQuery(id+"F4.wireOp",EDGE,"E26.top"),sQuery(id+"F4.wireOp",EDGE,"E26.left"),sQuery(id+"F4.wireOp",EDGE,"E26.right"),sQuery(id+"F4.wireOp",EDGE,"E27.bottom"),sQuery(id+"F4.wireOp",EDGE,"E27.top"),sQuery(id+"F4.wireOp",EDGE,"E27.right"),sQuery(id+"F4.wireOp",EDGE,"E28.top"),sQuery(id+"F4.wireOp",EDGE,"E28.left"),sQuery(id+"F4.wireOp",EDGE,"E28.right"),sQuery(id+"F4.wireOp",EDGE,"E29.bottom"),sQuery(id+"F4.wireOp",EDGE,"E29.top"),sQuery(id+"F4.wireOp",EDGE,"E29.right")])],"isStart":false}),"instanceName":"1"});
            mirror(context, id + "F9", {"operationType" : NewBodyOperationType.ADD, "entities" : qUnion([Q0]), "mirrorPlane" : qUnion([Q1])});
        }
        {
            var Q0;
            Q0=makeQuery(id+"F9.opPattern","COPY",FACE,{"derivedFrom":makeQuery(id+"F8.opPattern","COPY",FACE,{"derivedFrom":makeQuery(id+"F3.opExtrude","SWEPT_FACE",FACE,{"disambiguationData":[OSD([sQuery(id+"F2.wireOp",EDGE,"E14.right")])]}),"instanceName":"1"}),"instanceName":"1"});
            var Q1;
            Q1=makeQuery(id+"F8.opPattern","COPY",FACE,{"derivedFrom":makeQuery(id+"F3.opExtrude","SWEPT_FACE",FACE,{"disambiguationData":[OSD([sQuery(id+"F2.wireOp",EDGE,"E14.right")])]}),"instanceName":"1"});
            extrude(context, id + "F10", {"entities" : qUnion([Q0, Q1]), "operationType" : NewBodyOperationType.ADD, "depth" : 5.5 * mm, "offsetDistance" : 25 * mm});
        }
    });
